# Revit family: Cleanout-Floor-WATTS-CO12-SQ_Series
name_source: partatom
category: Plumbing Fixtures
units: mm (PartAtom-declared; Revit-internal decimal feet)

## family parameters
Cut with Voids When Loaded = No
Host = Face
OmniClass Number = 23.45.55.21
OmniClass Title = Drains (Wastes)
Part Type = Normal
Room Calculation Point = No
Round Connector Dimension = Use Radius
Shared = No

## types (6) — shared parameters
-DI Ductile Iron Top = No
-NB Nickel Bronze Top = Yes
-SS Stainless Steel Top = No
-VP Vandal Proof Screws = No
Assembly Code = D2030300
Body Length = 2"
Body Radius = 2 1/2"
CW Connection = No
Country = United States
Default Elevation = 0"
Description = PVC/ABS Adjustable Floor Cleanout w/Square Top
Flange Collar Radius = 2 13/16"
Flange Radius = 3 3/16"
Flange Thickness = 5/16"
Grate Height = 7/8"
Grate Height Constraint = 7/8"
Grate Width = 5 1/8"
HW Connection = No
Installation Type = Floor Mounted
Manufacturer = WATTS
Manufacturer Product Line = Drainage Products
Outlet Length = 2"
Product Documentation Link = https://www.watts.com
Product Page URL = https://www.watts.com
Region = North America
Revised Date = 02/07/2023
Top Material = Metal-WATTS-Nickel Bronze
URL = http://www.watts.com
Vent Connection = No
Waste Connection = Yes
zero-valued in all types: CWFU, HWFU, WFU

## per-type parameters (varying)
| type | Connection Description | Connection Size | Finish | Material | Outlet Radius |
| CO12-SQ-4ABS-NB | 4" ABS Connection Outlet | 4" | Plastic-WATTS-ABS | Plastic-WATTS-ABS | 2" |
| CO12-SQ-3ABS-NB | 3" ABS Connection Outlet | 3" | Plastic-WATTS-ABS | Plastic-WATTS-ABS | 1 1/2" |
| CO12-SQ-2ABS-NB | 2" ABS Connection Outlet | 2" | Plastic-WATTS-ABS | Plastic-WATTS-ABS | 1" |
| CO12-SQ-2PVC-NB | 2" PVC Connection Outlet | 2" | Plastic-WATTS-PVC | Plastic-WATTS-PVC | 1" |
| CO12-SQ-3PVC-NB | 3" PVC Connection Outlet | 3" | Plastic-WATTS-PVC | Plastic-WATTS-PVC | 1 1/2" |
| CO12-SQ-4PVC-NB | 4" PVC Connection Outlet | 4" | Plastic-WATTS-PVC | Plastic-WATTS-PVC | 2" |

note: column(s) folded — value = type name in every type: Model

## geometry (parser evidence)
native form markers: Sweep x3
no freeform markers — native parametric forms only
